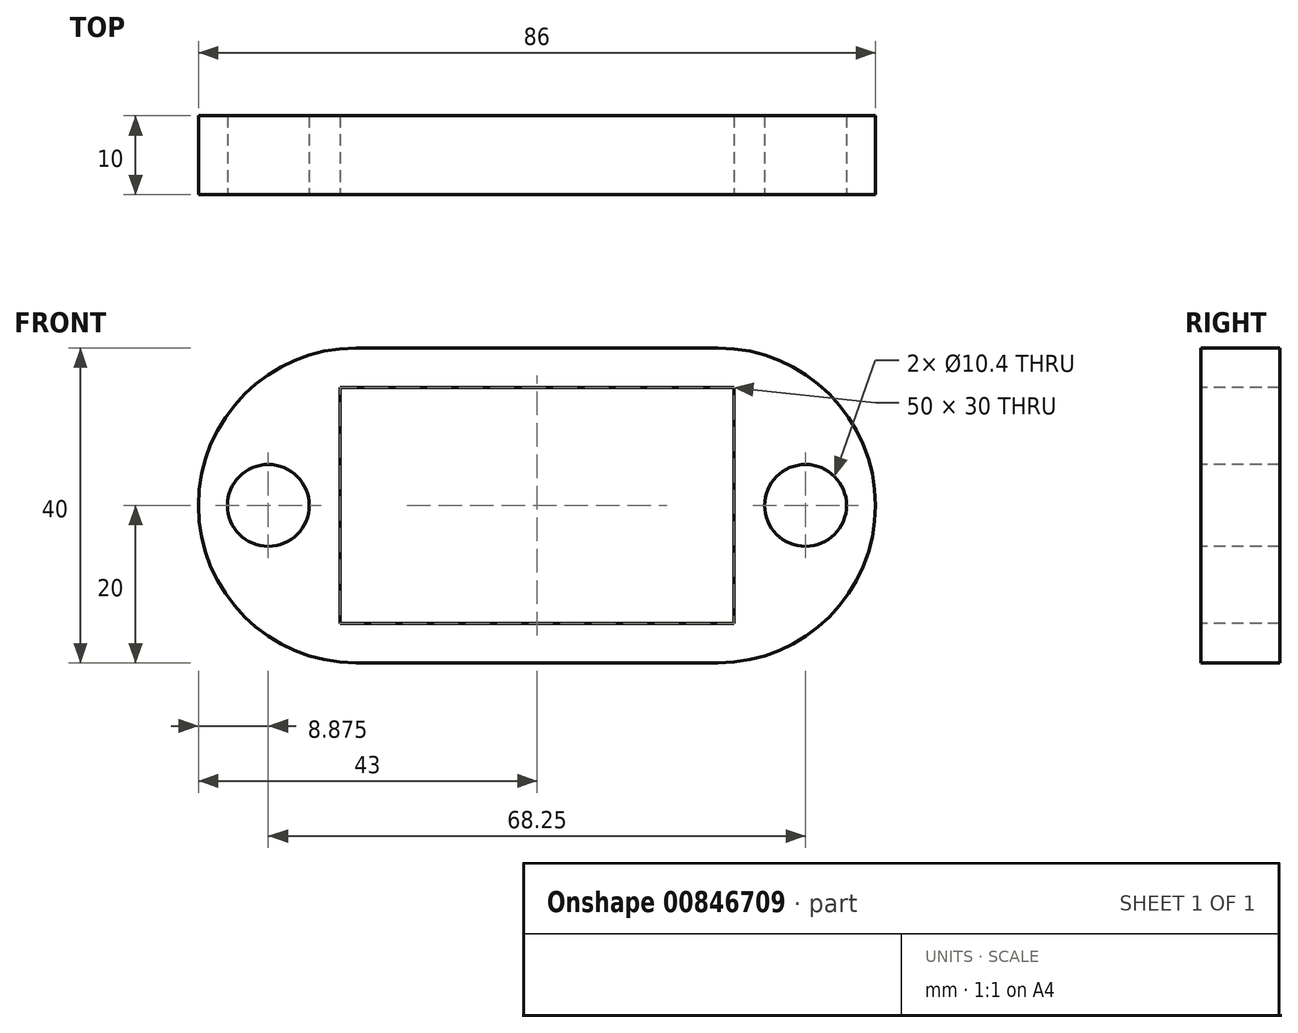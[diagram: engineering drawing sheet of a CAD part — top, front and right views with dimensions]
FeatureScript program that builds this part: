
annotation { "Feature Type Name" : "Feature", "Feature Type Description" : "" }
export const myFeature = defineFeature(function(context is Context, id is Id, definition is map)
    precondition{}
    {
        {
            var Q0;
            Q0=qCreatedBy(makeId("Front.planeOp"),FACE);
            var sketch = newSketch(context, id + "F0", { "sketchPlane" : qUnion([Q0])});
            skLineSegment(sketch, "E0.bottom", {"start": v(43, 20) * mm, "end": v(-43, 20) * mm});
            skLineSegment(sketch, "E0.top", {"start": v(43, -20) * mm, "end": v(-43, -20) * mm});
            skLineSegment(sketch, "E0.left", {"start": v(43, 20) * mm, "end": v(43, -20) * mm});
            skLineSegment(sketch, "E0.right", {"start": v(-43, 20) * mm, "end": v(-43, -20) * mm});
            skPoint(sketch, "E0.middle", {"position": v(0, 0) * mm});
            skSolve(sketch);
        }
        {
            var Q0;
            Q0=makeQuery(id+"F0.imprint","IMPRINT",FACE,{"disambiguationData":[TD([[makeQuery(id+"F0.imprint","IMPRINT",EDGE,{"derivedFrom":sQuery(id+"F0.wireOp",EDGE,"E0.bottom")}),1.0]])]});
            extrude(context, id + "F1", {"entities" : qUnion([Q0]), "oppositeDirection" : true, "depth" : 10 * mm, "offsetDistance" : 25 * mm});
        }
        {
            var Q0;
            Q0=makeQuery(id+"F1.opExtrude","CAP_FACE",FACE,{"disambiguationData":[OSD([sQuery(id+"F0.wireOp",EDGE,"E0.bottom"),sQuery(id+"F0.wireOp",EDGE,"E0.top"),sQuery(id+"F0.wireOp",EDGE,"E0.left"),sQuery(id+"F0.wireOp",EDGE,"E0.right")])],"isStart":true});
            var sketch = newSketch(context, id + "F2", { "sketchPlane" : qUnion([Q0])});
            skLineSegment(sketch, "E1", {"start": v(-43, 0) * mm, "end": v(43, 0) * mm, "construction": true});
            skCircle(sketch, "E2", {"center": v(-34.12, 0) * mm, "radius": 5.2 * mm});
            skCircle(sketch, "E3", {"center": v(34.12, 0) * mm, "radius": 5.2 * mm});
            skSolve(sketch);
        }
        {
            var Q0;
            Q0=makeQuery(id+"F2.imprint","IMPRINT",FACE,{"disambiguationData":[TD([[makeQuery(id+"F2.imprint","IMPRINT",EDGE,{"derivedFrom":sQuery(id+"F2.wireOp",EDGE,"E2")}),1.0]])]});
            var Q1;
            Q1=makeQuery(id+"F2.imprint","IMPRINT",FACE,{"disambiguationData":[TD([[makeQuery(id+"F2.imprint","IMPRINT",EDGE,{"derivedFrom":sQuery(id+"F2.wireOp",EDGE,"E3")}),1.0]])]});
            extrude(context, id + "F3", {"entities" : qUnion([Q0, Q1]), "operationType" : NewBodyOperationType.REMOVE, "oppositeDirection" : true, "depth" : 25 * mm, "offsetDistance" : 25 * mm});
        }
        {
            var Q0;
            Q0=makeQuery(id+"F1.opExtrude","CAP_FACE",FACE,{"disambiguationData":[OSD([sQuery(id+"F0.wireOp",EDGE,"E0.bottom"),sQuery(id+"F0.wireOp",EDGE,"E0.top"),sQuery(id+"F0.wireOp",EDGE,"E0.left"),sQuery(id+"F0.wireOp",EDGE,"E0.right")])],"isStart":true});
            var sketch = newSketch(context, id + "F4", { "sketchPlane" : qUnion([Q0])});
            skLineSegment(sketch, "E4.bottom", {"start": v(25, 15) * mm, "end": v(-25, 15) * mm});
            skLineSegment(sketch, "E4.top", {"start": v(25, -15) * mm, "end": v(-25, -15) * mm});
            skLineSegment(sketch, "E4.left", {"start": v(25, 15) * mm, "end": v(25, -15) * mm});
            skLineSegment(sketch, "E4.right", {"start": v(-25, 15) * mm, "end": v(-25, -15) * mm});
            skPoint(sketch, "E4.middle", {"position": v(0, 0) * mm});
            skSolve(sketch);
        }
        {
            var Q0;
            Q0=makeQuery(id+"F4.imprint","IMPRINT",FACE,{"disambiguationData":[TD([[makeQuery(id+"F4.imprint","IMPRINT",EDGE,{"derivedFrom":sQuery(id+"F4.wireOp",EDGE,"E4.bottom")}),1.0]])]});
            extrude(context, id + "F5", {"entities" : qUnion([Q0]), "operationType" : NewBodyOperationType.REMOVE, "oppositeDirection" : true, "depth" : 25 * mm, "offsetDistance" : 25 * mm});
        }
        {
            var Q0;
            Q0=makeQuery(id+"F1.opExtrude","SWEPT_EDGE",EDGE,{"disambiguationData":[OSD([sQuery(id+"F0.wireOp",EDGE,"E0.bottom"),sQuery(id+"F0.wireOp",EDGE,"E0.right")])]});
            var Q1;
            Q1=makeQuery(id+"F1.opExtrude","SWEPT_EDGE",EDGE,{"disambiguationData":[OSD([sQuery(id+"F0.wireOp",EDGE,"E0.bottom"),sQuery(id+"F0.wireOp",EDGE,"E0.left")])]});
            var Q2;
            Q2=makeQuery(id+"F1.opExtrude","SWEPT_EDGE",EDGE,{"disambiguationData":[OSD([sQuery(id+"F0.wireOp",EDGE,"E0.top"),sQuery(id+"F0.wireOp",EDGE,"E0.left")])]});
            var Q3;
            Q3=makeQuery(id+"F1.opExtrude","SWEPT_EDGE",EDGE,{"disambiguationData":[OSD([sQuery(id+"F0.wireOp",EDGE,"E0.top"),sQuery(id+"F0.wireOp",EDGE,"E0.right")])]});
            fillet(context, id + "F6", {"entities" : qUnion([Q0, Q1, Q2, Q3]), "radius" : 20 * mm, "tangentPropagation" : true, "allowEdgeOverflow" : false});
        }
    });
